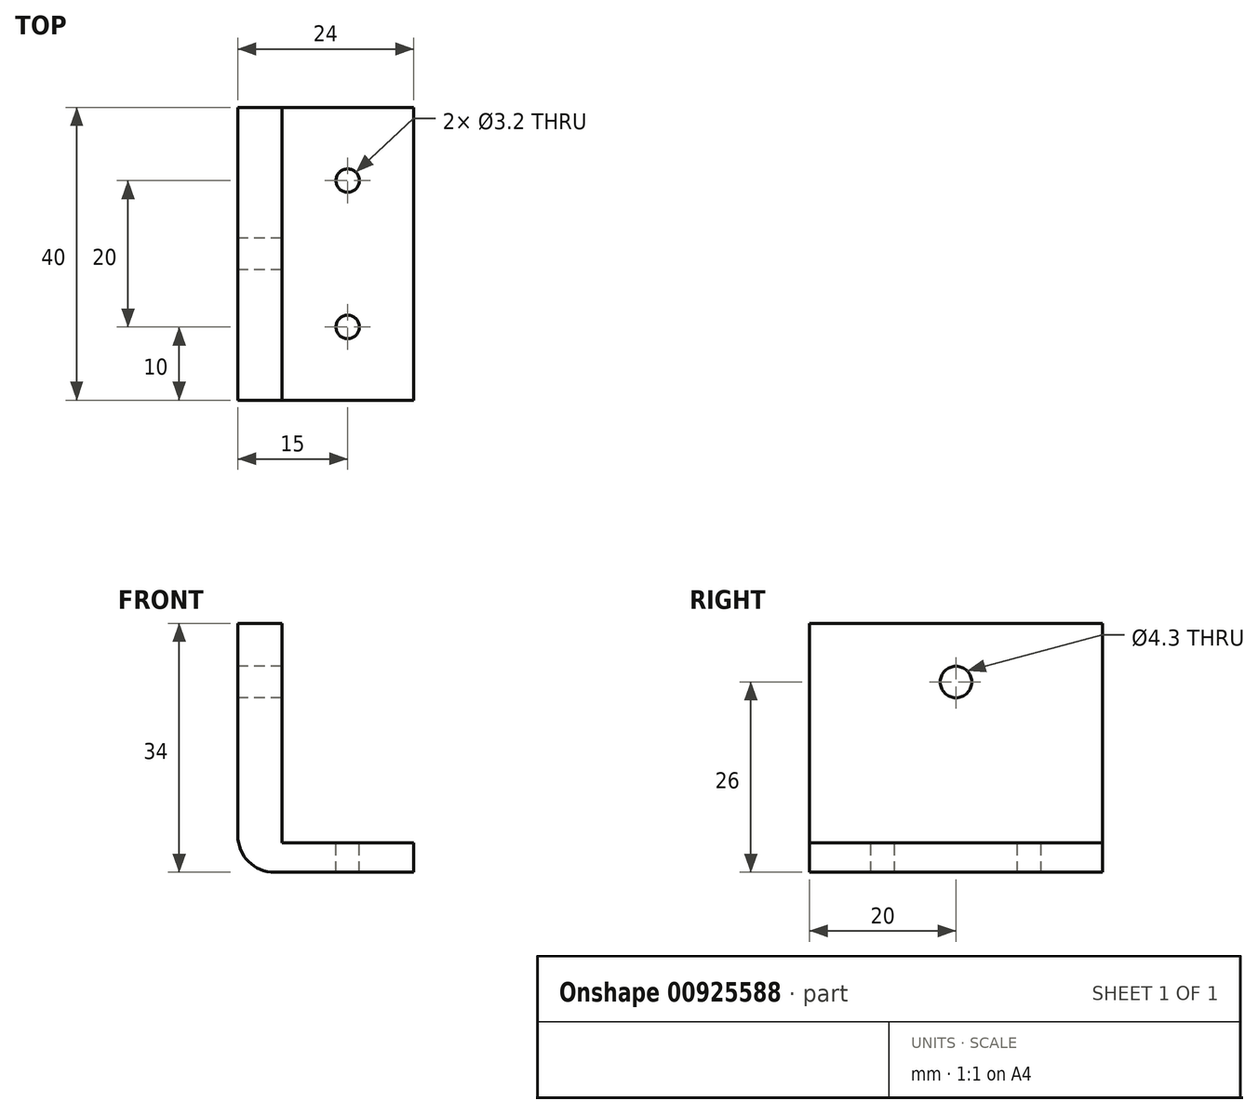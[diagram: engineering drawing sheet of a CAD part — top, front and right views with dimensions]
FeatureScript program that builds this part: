
annotation { "Feature Type Name" : "Feature", "Feature Type Description" : "" }
export const myFeature = defineFeature(function(context is Context, id is Id, definition is map)
    precondition{}
    {
        {
            var Q0;
            Q0=qCreatedBy(makeId("Front.planeOp"),FACE);
            var sketch = newSketch(context, id + "F0", { "sketchPlane" : qUnion([Q0])});
            skLineSegment(sketch, "E0.bottom", {"start": v(3, -15) * mm, "end": v(-3, -15) * mm});
            skLineSegment(sketch, "E0.top", {"start": v(3, 15) * mm, "end": v(-3, 15) * mm});
            skLineSegment(sketch, "E0.left", {"start": v(3, -15) * mm, "end": v(3, 15) * mm});
            skLineSegment(sketch, "E0.right", {"start": v(-3, -15) * mm, "end": v(-3, 15) * mm});
            skPoint(sketch, "E0.middle", {"position": v(0, 0) * mm});
            skLineSegment(sketch, "E1.bottom", {"start": v(-3, -15) * mm, "end": v(21, -15) * mm});
            skLineSegment(sketch, "E1.top", {"start": v(-3, -19) * mm, "end": v(21, -19) * mm});
            skLineSegment(sketch, "E1.left", {"start": v(-3, -15) * mm, "end": v(-3, -19) * mm});
            skLineSegment(sketch, "E1.right", {"start": v(21, -15) * mm, "end": v(21, -19) * mm});
            skSolve(sketch);
        }
        {
            var Q0;
            Q0 = qSketchRegion(id + "F0", true);
            extrude(context, id + "F1", {"entities" : qUnion([Q0]), "depth" : 40 * mm, "offsetDistance" : 25 * mm});
        }
        {
            var Q0;
            Q0=makeQuery(id+"F1.opExtrude","SWEPT_EDGE",EDGE,{"disambiguationData":[OSD([sQuery(id+"F0.wireOp",EDGE,"E1.top"),sQuery(id+"F0.wireOp",EDGE,"E1.left")])]});
            fillet(context, id + "F2", {"entities" : qUnion([Q0]), "radius" : 5 * mm, "tangentPropagation" : true, "allowEdgeOverflow" : false});
        }
        {
            var Q0;
            Q0=makeQuery(id+"F1.opExtrude","SWEPT_FACE",FACE,{"disambiguationData":[OSD([sQuery(id+"F0.wireOp",EDGE,"E0.right"),sQuery(id+"F0.wireOp",EDGE,"E1.left")])]});
            var sketch = newSketch(context, id + "F3", { "sketchPlane" : qUnion([Q0])});
            skCircle(sketch, "E2", {"center": v(20, 7) * mm, "radius": 2.15 * mm});
            skPoint(sketch, "E2.centerSnap0", {"position": v(20, 15) * mm});
            skSolve(sketch);
        }
        {
            var Q0;
            Q0 = qSketchRegion(id + "F3", true);
            extrude(context, id + "F4", {"entities" : qUnion([Q0]), "operationType" : NewBodyOperationType.REMOVE, "oppositeDirection" : true, "depth" : 25 * mm, "offsetDistance" : 25 * mm});
        }
        {
            var Q0;
            Q0=makeQuery(id+"F1.opExtrude","SWEPT_FACE",FACE,{"disambiguationData":[OSD([sQuery(id+"F0.wireOp",EDGE,"E1.bottom")])]});
            var sketch = newSketch(context, id + "F5", { "sketchPlane" : qUnion([Q0])});
            skLineSegment(sketch, "E3", {"start": v(12, 0) * mm, "end": v(12, -40) * mm, "construction": true});
            skCircle(sketch, "E4", {"center": v(12, -10) * mm, "radius": 1.6 * mm});
            skCircle(sketch, "E5", {"center": v(12, -30) * mm, "radius": 1.6 * mm});
            skSolve(sketch);
        }
        {
            var Q0;
            Q0 = qSketchRegion(id + "F5", true);
            extrude(context, id + "F6", {"entities" : qUnion([Q0]), "operationType" : NewBodyOperationType.REMOVE, "oppositeDirection" : true, "depth" : 25 * mm, "offsetDistance" : 25 * mm});
        }
    });
